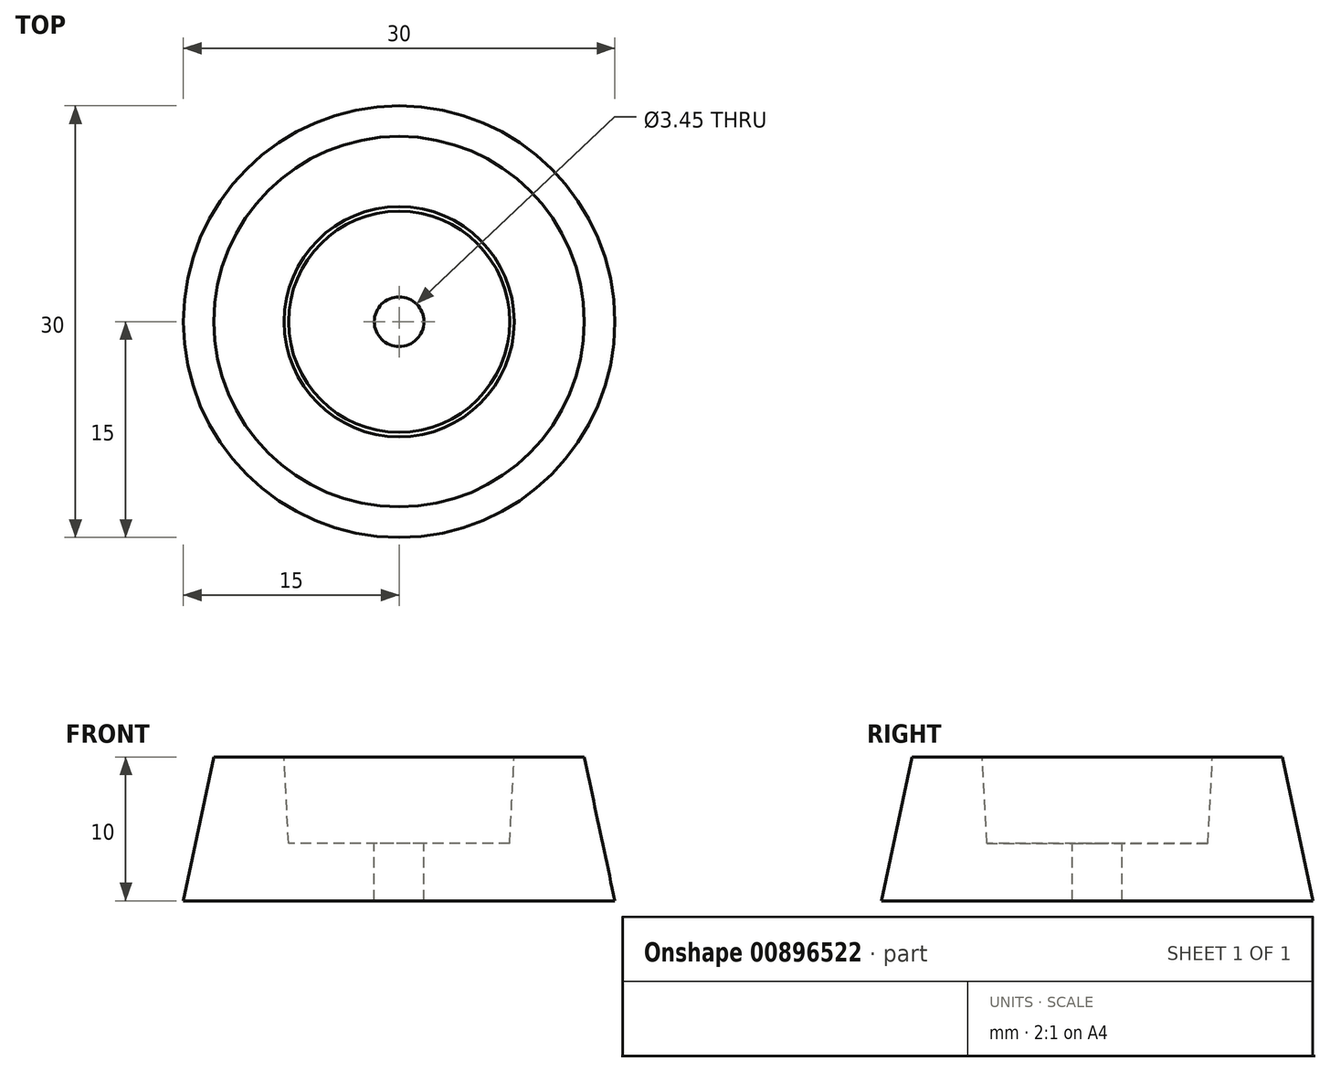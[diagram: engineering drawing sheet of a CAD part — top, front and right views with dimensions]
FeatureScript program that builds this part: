
annotation { "Feature Type Name" : "Feature", "Feature Type Description" : "" }
export const myFeature = defineFeature(function(context is Context, id is Id, definition is map)
    precondition{}
    {
        {
            var Q0;
            Q0=qCreatedBy(makeId("Top.planeOp"),FACE);
            var sketch = newSketch(context, id + "F0", { "sketchPlane" : qUnion([Q0])});
            skCircle(sketch, "E0", {"center": v(0, 0) * mm, "radius": 15 * mm});
            skSolve(sketch);
        }
        {
            var Q0;
            Q0 = qSketchRegion(id + "F0", true);
            extrude(context, id + "F1", {"entities" : qUnion([Q0]), "depth" : 10 * mm, "offsetDistance" : 25 * mm, "hasDraft" : true, "draftAngle" : 12 * degree, "draftPullDirection" : true});
        }
        {
            var Q0;
            Q0=makeQuery(id+"F1.opExtrude","CAP_FACE",FACE,{"disambiguationData":[OSD([sQuery(id+"F0.wireOp",EDGE,"E0")])],"isStart":false});
            var sketch = newSketch(context, id + "F2", { "sketchPlane" : qUnion([Q0])});
            skCircle(sketch, "E1", {"center": v(0, 0) * mm, "radius": 8 * mm});
            skSolve(sketch);
        }
        {
            var Q0;
            Q0 = qSketchRegion(id + "F2", true);
            extrude(context, id + "F3", {"entities" : qUnion([Q0]), "operationType" : NewBodyOperationType.REMOVE, "oppositeDirection" : true, "depth" : 6 * mm, "offsetDistance" : 25 * mm, "hasDraft" : true, "draftAngle" : 3 * degree, "draftPullDirection" : true});
        }
        {
            var Q0;
            Q0=makeQuery(id+"F3.boolean.opBoolean","COPY",FACE,{"derivedFrom":makeQuery(id+"F3.opExtrude","CAP_FACE",FACE,{"disambiguationData":[OSD([sQuery(id+"F2.wireOp",EDGE,"E1")])],"isStart":false})});
            var sketch = newSketch(context, id + "F4", { "sketchPlane" : qUnion([Q0])});
            skCircle(sketch, "E2", {"center": v(0, 0) * mm, "radius": 1.73 * mm});
            skSolve(sketch);
        }
        {
            var Q0;
            Q0 = qSketchRegion(id + "F4", true);
            extrude(context, id + "F5", {"entities" : qUnion([Q0]), "operationType" : NewBodyOperationType.REMOVE, "endBound" : BoundingType.UP_TO_NEXT, "oppositeDirection" : true, "depth" : 25 * mm, "offsetDistance" : 25 * mm});
        }
    });
